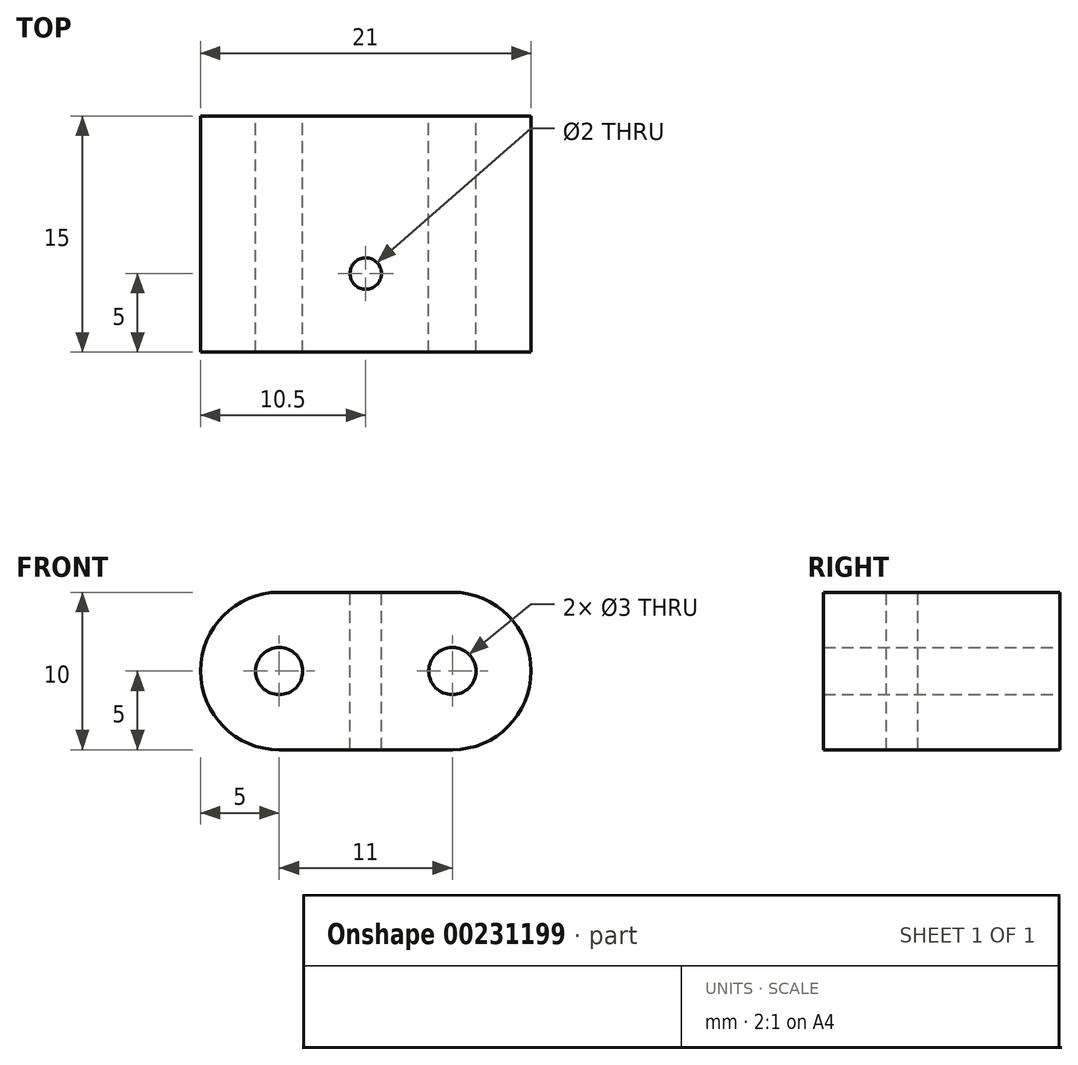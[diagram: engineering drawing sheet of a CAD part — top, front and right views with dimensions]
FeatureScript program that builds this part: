
annotation { "Feature Type Name" : "Feature", "Feature Type Description" : "" }
export const myFeature = defineFeature(function(context is Context, id is Id, definition is map)
    precondition{}
    {
        {
            var Q0;
            Q0=qCreatedBy(makeId("Front.planeOp"),FACE);
            var sketch = newSketch(context, id + "F0", { "sketchPlane" : qUnion([Q0])});
            skLineSegment(sketch, "E0.bottom", {"start": v(-10.5, 0) * mm, "end": v(10.5, 0) * mm});
            skLineSegment(sketch, "E0.top", {"start": v(-10.5, -10) * mm, "end": v(10.5, -10) * mm});
            skLineSegment(sketch, "E0.left", {"start": v(-10.5, 0) * mm, "end": v(-10.5, -10) * mm});
            skLineSegment(sketch, "E0.right", {"start": v(10.5, 0) * mm, "end": v(10.5, -10) * mm});
            skCircle(sketch, "E1", {"center": v(-5.5, -5) * mm, "radius": 5 * mm});
            skPoint(sketch, "E1.centerSnap0", {"position": v(-10.5, -5) * mm});
            skCircle(sketch, "E2", {"center": v(5.5, -5) * mm, "radius": 5 * mm});
            skCircle(sketch, "E3", {"center": v(-5.5, -5) * mm, "radius": 1.5 * mm});
            skCircle(sketch, "E4", {"center": v(5.5, -5) * mm, "radius": 1.5 * mm});
            skSolve(sketch);
        }
        {
            var Q0;
            {var subQ0=sQuery(id+"F0.wireOp",EDGE,"E1");var subQ1=makeQuery(id+"F0.imprint","INTERSECT",VERTEX,{"derivedFrom":[sQuery(id+"F0.wireOp",EDGE,"E0.bottom"),subQ0]});Q0=makeQuery(id+"F0.imprint","IMPRINT",FACE,{"disambiguationData":[TD([[makeQuery(id+"F0.imprint","IMPRINT",EDGE,{"disambiguationData":[TD([[subQ1,-1.0]])],"derivedFrom":subQ0}),1.0]])]});}
            var Q1;
            {var subQ0=sQuery(id+"F0.wireOp",EDGE,"E1");var subQ1=sQuery(id+"F0.wireOp",EDGE,"E0.bottom");var subQ2=makeQuery(id+"F0.imprint","INTERSECT",VERTEX,{"derivedFrom":[subQ1,subQ0]});Q1=makeQuery(id+"F0.imprint","IMPRINT",FACE,{"disambiguationData":[TD([[makeQuery(id+"F0.imprint","IMPRINT",EDGE,{"disambiguationData":[TD([[subQ2,-1.0]])],"derivedFrom":subQ1}),-1.0]])]});}
            var Q2;
            {var subQ0=sQuery(id+"F0.wireOp",EDGE,"E2");var subQ1=makeQuery(id+"F0.imprint","INTERSECT",VERTEX,{"derivedFrom":[sQuery(id+"F0.wireOp",EDGE,"E0.bottom"),subQ0]});Q2=makeQuery(id+"F0.imprint","IMPRINT",FACE,{"disambiguationData":[TD([[makeQuery(id+"F0.imprint","IMPRINT",EDGE,{"disambiguationData":[TD([[subQ1,1.0]])],"derivedFrom":subQ0}),1.0]])]});}
            extrude(context, id + "F1", {"entities" : qUnion([Q0, Q1, Q2]), "depth" : 15 * mm});
        }
        {
            var Q0;
            Q0=qCreatedBy(makeId("Top.planeOp"),FACE);
            var sketch = newSketch(context, id + "F2", { "sketchPlane" : qUnion([Q0])});
            skCircle(sketch, "E5", {"center": v(0, -10) * mm, "radius": 1 * mm});
            skSolve(sketch);
        }
        {
            var Q0;
            Q0=makeQuery(id+"F2.imprint","IMPRINT",FACE,{"disambiguationData":[TD([[makeQuery(id+"F2.imprint","IMPRINT",EDGE,{"derivedFrom":sQuery(id+"F2.wireOp",EDGE,"E5")}),1.0]])]});
            extrude(context, id + "F3", {"entities" : qUnion([Q0]), "operationType" : NewBodyOperationType.REMOVE, "oppositeDirection" : true, "depth" : 10 * mm});
        }
    });
